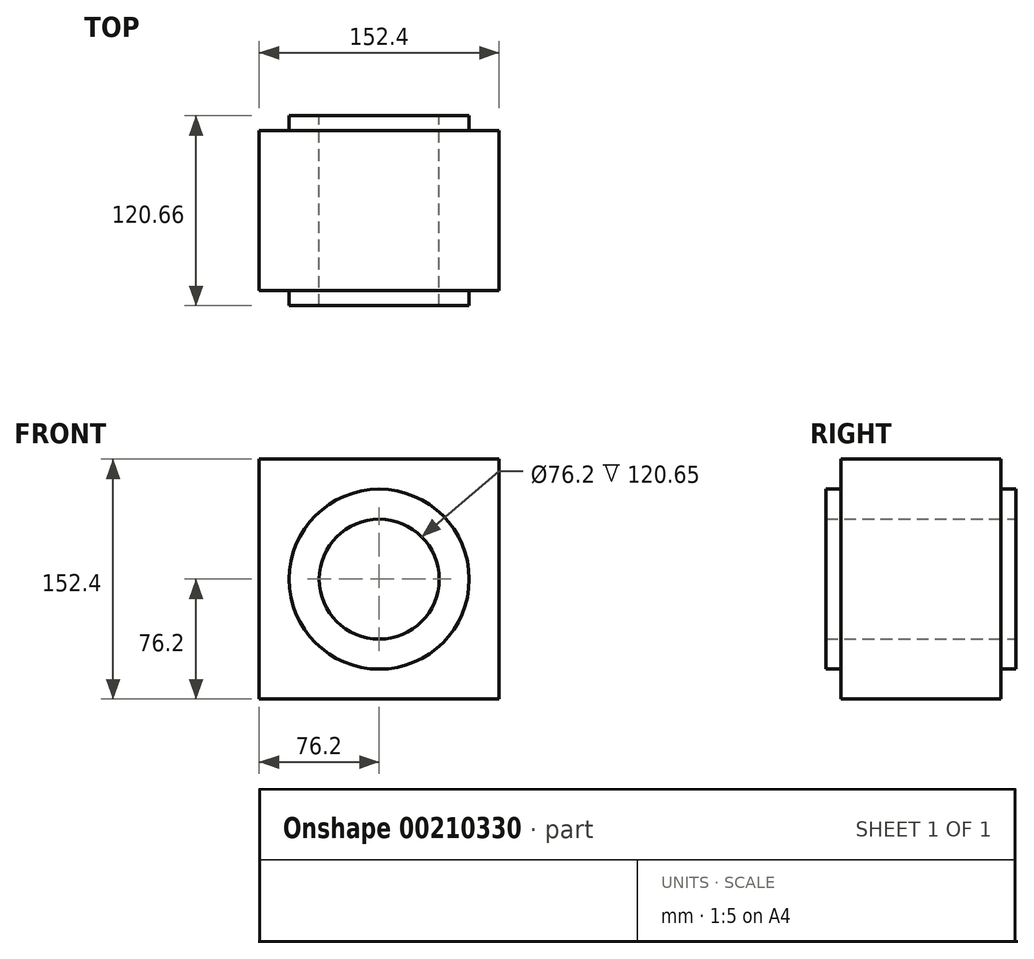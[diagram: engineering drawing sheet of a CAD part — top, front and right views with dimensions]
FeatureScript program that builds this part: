
annotation { "Feature Type Name" : "Feature", "Feature Type Description" : "" }
export const myFeature = defineFeature(function(context is Context, id is Id, definition is map)
    precondition{}
    {
        {
            var Q0;
            Q0=qCreatedBy(makeId("Front.planeOp"),FACE);
            var sketch = newSketch(context, id + "F0", { "sketchPlane" : qUnion([Q0])});
            skLineSegment(sketch, "E0.bottom", {"start": v(76.2, 76.2) * mm, "end": v(-76.2, 76.2) * mm});
            skLineSegment(sketch, "E0.top", {"start": v(76.2, -76.2) * mm, "end": v(-76.2, -76.2) * mm});
            skLineSegment(sketch, "E0.left", {"start": v(76.2, 76.2) * mm, "end": v(76.2, -76.2) * mm});
            skLineSegment(sketch, "E0.right", {"start": v(-76.2, 76.2) * mm, "end": v(-76.2, -76.2) * mm});
            skPoint(sketch, "E0.middle", {"position": v(0, 0) * mm});
            skCircle(sketch, "E1", {"center": v(0, 0) * mm, "radius": 38.1 * mm});
            skSolve(sketch);
        }
        {
            var Q0;
            Q0 = qSketchRegion(id + "F0", true);
            extrude(context, id + "F1", {"entities" : qUnion([Q0]), "depth" : 101.6 * mm});
        }
        {
            var Q0;
            Q0=makeQuery(id+"F1.opExtrude","CAP_FACE",FACE,{"disambiguationData":[OSD([sQuery(id+"F0.wireOp",EDGE,"E0.bottom"),sQuery(id+"F0.wireOp",EDGE,"E0.top"),sQuery(id+"F0.wireOp",EDGE,"E0.left"),sQuery(id+"F0.wireOp",EDGE,"E0.right"),sQuery(id+"F0.wireOp",EDGE,"E1")])],"isStart":false});
            var sketch = newSketch(context, id + "F2", { "sketchPlane" : qUnion([Q0])});
            skCircle(sketch, "E2", {"center": v(0, 0) * mm, "radius": 57.15 * mm});
            skCircle(sketch, "E3", {"center": v(0, 0) * mm, "radius": 38.1 * mm});
            skSolve(sketch);
        }
        {
            var Q0;
            Q0 = qSketchRegion(id + "F2", true);
            extrude(context, id + "F3", {"entities" : qUnion([Q0]), "operationType" : NewBodyOperationType.ADD, "depth" : 9.52 * mm});
        }
        {
            var Q0;
            Q0=makeQuery(id+"F1.opExtrude","CAP_FACE",FACE,{"disambiguationData":[OSD([sQuery(id+"F0.wireOp",EDGE,"E0.bottom"),sQuery(id+"F0.wireOp",EDGE,"E0.top"),sQuery(id+"F0.wireOp",EDGE,"E0.left"),sQuery(id+"F0.wireOp",EDGE,"E0.right"),sQuery(id+"F0.wireOp",EDGE,"E1")])],"isStart":true});
            var sketch = newSketch(context, id + "F4", { "sketchPlane" : qUnion([Q0])});
            skCircle(sketch, "E4", {"center": v(0, 0) * mm, "radius": 57.15 * mm});
            skCircle(sketch, "E5", {"center": v(0, 0) * mm, "radius": 38.1 * mm});
            skSolve(sketch);
        }
        {
            var Q0;
            Q0 = qSketchRegion(id + "F4", true);
            extrude(context, id + "F5", {"entities" : qUnion([Q0]), "operationType" : NewBodyOperationType.ADD, "depth" : 9.52 * mm});
        }
    });
